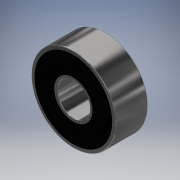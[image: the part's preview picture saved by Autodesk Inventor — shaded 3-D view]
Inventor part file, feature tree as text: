
AUTODESK INVENTOR PART (.ipt)
format: ipt  version: 2017.1 (Build 211199000, 199)  size: 195,584 bytes
history: native  units: in
note: dims shown in document units (in); Inventor stores cm internally (conversion verified against a paired STEP export)
features: sketch x2, extrude x1, fillet x1, revolve x1, plane x1, mirror x1
ambient origin geometry x8: Origin, YZ Plane, XZ Plane, XY Plane, X Axis, Y Axis, Z Axis, Center Point
bodies: Solid1 (feature_tree)
feature tree (7):
  extrude  "Extrusion1"  Depth=0.3937in
  fillet  "Fillet1"  Radius=0.3937in
  revolve  "Revolution1"  Angle=90.0deg
  plane  "Work Plane2"
  mirror  "Mirror2"
  sketch  "Sketch1"  dims[d0=0.3937in d1=1.0236in d2=0.3937in d3=0.0in]
  sketch  "Sketch2"  dims[d4=0.0118in d5=90.0deg d6=0.0197in d7=-0.1969in]
